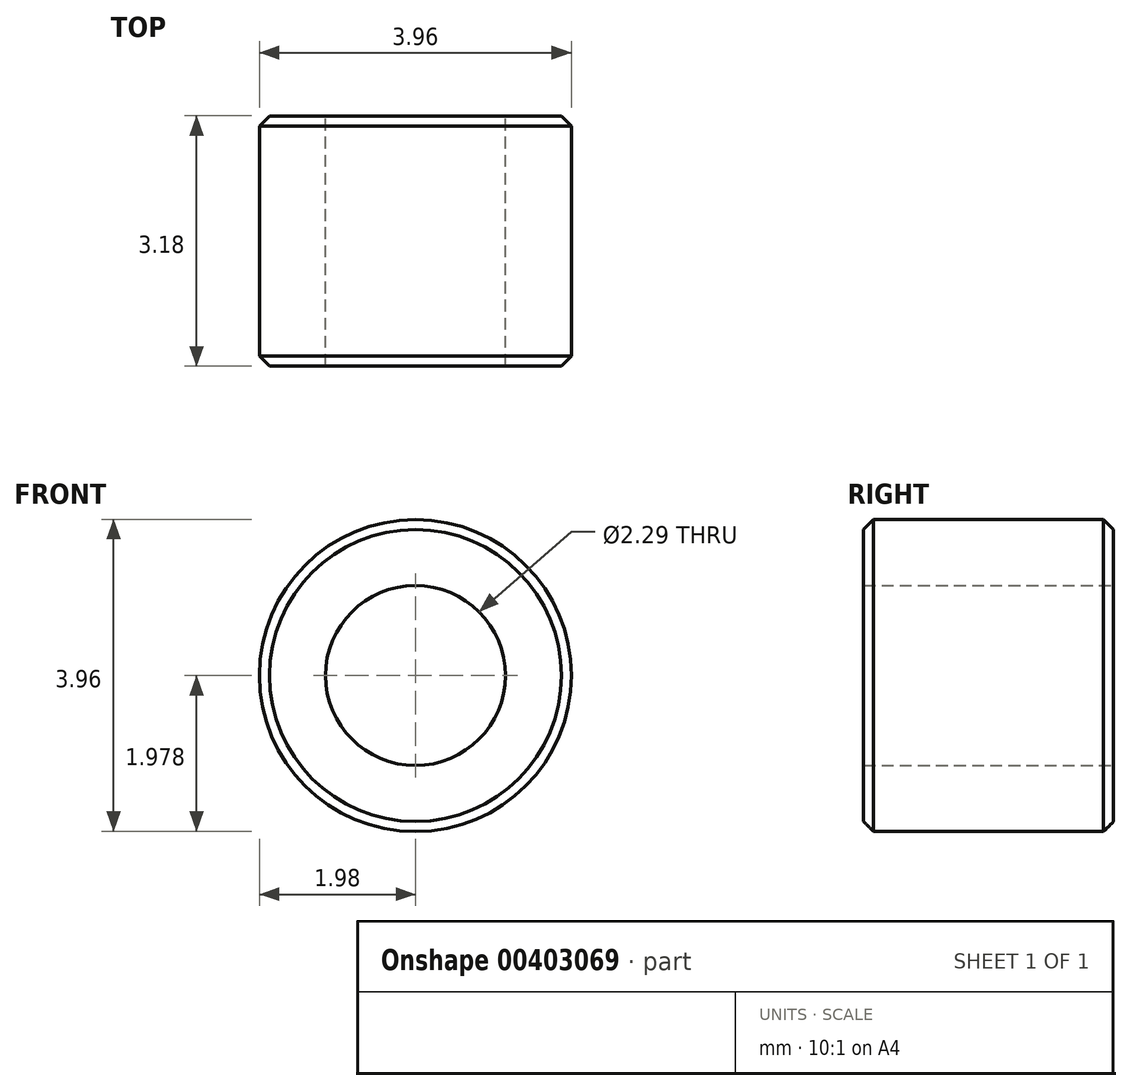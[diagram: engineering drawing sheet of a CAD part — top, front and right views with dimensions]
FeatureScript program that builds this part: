
annotation { "Feature Type Name" : "Feature", "Feature Type Description" : "" }
export const myFeature = defineFeature(function(context is Context, id is Id, definition is map)
    precondition{}
    {
        {
            var Q0;
            Q0=qCreatedBy(makeId("Front.planeOp"),FACE);
            var sketch = newSketch(context, id + "F0", { "sketchPlane" : qUnion([Q0])});
            skCircle(sketch, "E0", {"center": v(0, 7.96) * mm, "radius": 1.98 * mm});
            skLineSegment(sketch, "E1.left", {"start": v(-1.59, -5.4) * mm, "end": v(-1.59, 6.77) * mm});
            skLineSegment(sketch, "E1.right", {"start": v(1.59, -5.4) * mm, "end": v(1.59, 6.77) * mm});
            skArc(sketch, "E2", {"start": v(-1.58, -5.4) * mm, "mid": v(0, -7.13) * mm, "end": v(1.58, -5.4) * mm});
            skLineSegment(sketch, "E3", {"start": v(-1.59, -5.4) * mm, "end": v(-1.58, -5.4) * mm});
            skLineSegment(sketch, "E4.trimOffspring", {"start": v(1.58, -5.4) * mm, "end": v(1.59, -5.4) * mm});
            skCircle(sketch, "E5", {"center": v(0, 7.96) * mm, "radius": 1.14 * mm});
            skSolve(sketch);
        }
        {
            var Q0;
            Q0=makeQuery(id+"F0.imprint","IMPRINT",FACE,{"disambiguationData":[TD([[makeQuery(id+"F0.imprint","IMPRINT",EDGE,{"derivedFrom":sQuery(id+"F0.wireOp",EDGE,"E5")}),-1.0]])]});
            extrude(context, id + "F1", {"entities" : qUnion([Q0]), "endBound" : BoundingType.SYMMETRIC, "depth" : 3.17 * mm});
        }
        {
            var Q0;
            Q0=makeQuery(id+"F1.opExtrude","CAP_EDGE",EDGE,{"disambiguationData":[OSD([sQuery(id+"F0.wireOp",EDGE,"E0")])],"isStart":false});
            chamfer(context, id + "F2", {"entities" : qUnion([Q0]), "chamferType" : ChamferType.TWO_OFFSETS, "width1" : 0.13 * mm, "oppositeDirection" : false, "width2" : 0.13 * mm, "tangentPropagation" : true});
        }
        {
            var Q0;
            Q0=makeQuery(id+"F1.opExtrude","CAP_EDGE",EDGE,{"disambiguationData":[OSD([sQuery(id+"F0.wireOp",EDGE,"E0")])],"isStart":true});
            chamfer(context, id + "F3", {"entities" : qUnion([Q0]), "chamferType" : ChamferType.TWO_OFFSETS, "width1" : 0.13 * mm, "oppositeDirection" : false, "width2" : 0.13 * mm});
        }
    });
